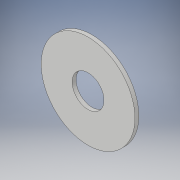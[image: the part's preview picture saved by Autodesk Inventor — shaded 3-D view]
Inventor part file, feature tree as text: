
AUTODESK INVENTOR PART (.ipt)
format: ipt  version: 2018 (Build 220112000, 112)  size: 98,304 bytes
history: native  units: in
note: dims shown in document units (in); Inventor stores cm internally (conversion verified against a paired STEP export)
features: extrude x1, sketch x1
ambient origin geometry x8: Origin, YZ Plane, XZ Plane, XY Plane, X Axis, Y Axis, Z Axis, Center Point
bodies: Solid1 (feature_tree)
feature tree (2):
  extrude  "Extrusion1"  Depth=0.0312in
  sketch  "Sketch1"  dims[d0=0.75in d1=0.255in d2=0.0312in d3=0.0in]
